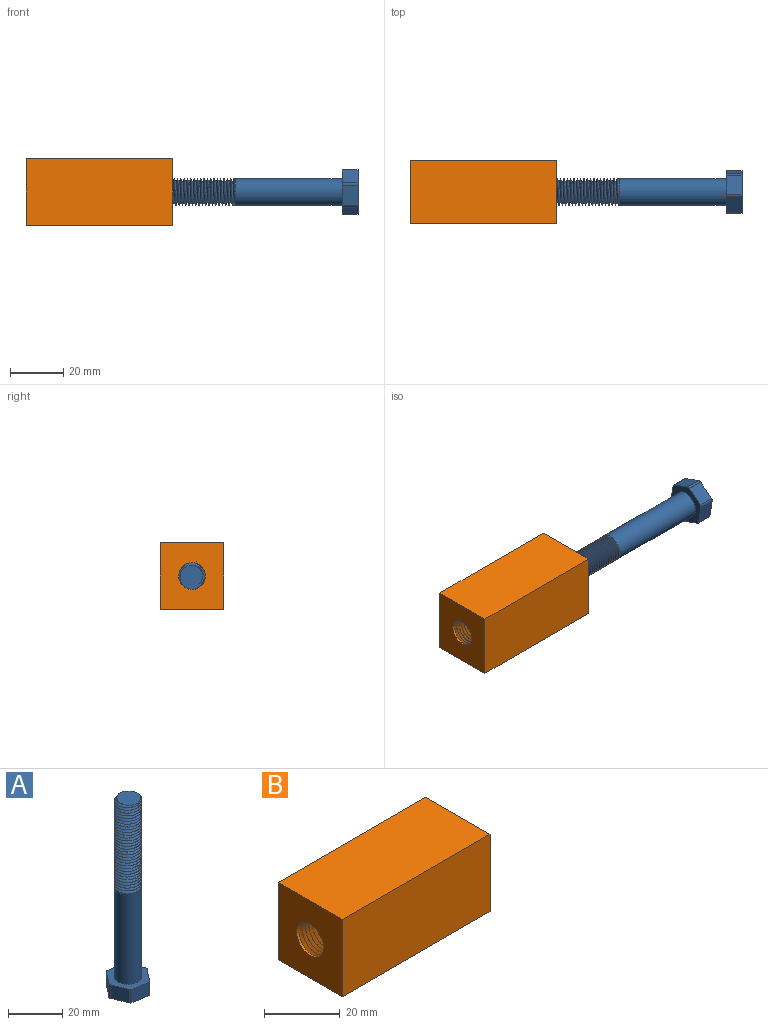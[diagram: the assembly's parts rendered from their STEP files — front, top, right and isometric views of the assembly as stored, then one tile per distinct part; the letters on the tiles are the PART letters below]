
ASSEMBLY  parts=2 mates=1
PART A: 21 faces, bbox 17.7x16.8x87.6 mm
  f0: cylinder r=5mm len=40mm, axis (0,0,-1), area -150.1mm2, adj f16,f17,f18,f19,f20
  f1: plane 7.43x6mm, normal (-0.14,-0.99,0), area 45mm2, adj f7,f8,f9,f14
  f2: plane 6x5.89mm, normal (0.78,-0.62,0), area 45mm2, adj f7,f8,f9,f10
  f3: plane 6.98x6mm, normal (0.93,0.37,0), area 45mm2, adj f7,f8,f10,f11
  f4: plane 7.43x6mm, normal (0.14,0.99,0), area 45mm2, adj f7,f8,f11,f12
  f5: plane 6x5.89mm, normal (-0.78,0.62,0), area 45mm2, adj f7,f8,f12,f13
  f6: plane 6.98x6mm, normal (-0.93,-0.37,0), area 45mm2, adj f7,f8,f13,f14
  f7: plane 16.85x15.95mm, normal (0,0,1), area 114.4mm2, adj f1,f2,f3,f4,f5,f6,f9,f10
  f8: plane 16.85x15.95mm, normal (0,0,-1), area 194.5mm2, adj f1,f2,f3,f4,f5,f6,f9,f10
  f9: cylinder r=1mm len=6mm, axis (0,0,-1), area 6.3mm2, adj f1,f2,f7,f8
  f10: cylinder r=1mm len=6mm, axis (0,0,-1), area 6.3mm2, adj f2,f3,f7,f8
  f11: cylinder r=1mm len=6mm, axis (0,0,-1), area 6.3mm2, adj f3,f4,f7,f8
  f12: cylinder r=1mm len=6mm, axis (0,0,-1), area 6.3mm2, adj f4,f5,f7,f8
  f13: cylinder r=1mm len=6mm, axis (0,0,-1), area 6.3mm2, adj f5,f6,f7,f8
  f14: cylinder r=1mm len=6mm, axis (0,0,-1), area 6.3mm2, adj f1,f6,f7,f8
  f15: cylinder r=5.05mm len=40mm, axis (0,0,-1), area 1269.2mm2, adj f7,f16
  f16: plane 10.1x10.1mm, normal (0,0,1), area 1.6mm2, adj f0,f15
  f17: plane 9.9x9.88mm, normal (0,0,1), area 64mm2, adj f0,f19,f20
  f18: plane 1.2x1.04mm, normal (0,1,0), area 0.6mm2, adj f0,f19,f20
  f19: bspline ~40.6x11.55mm, area 1070.9mm2, adj f0,f17,f18,f20
  f20: bspline ~40.18x11.55mm, area 1058mm2, adj f0,f17,f18,f19
PART B: 19 faces, bbox 57x24.8x25.8 mm
  f0: cylinder r=5.05mm len=55.25mm, axis (-1,0,0), area -140.6mm2, adj f2,f4,f7,f8,f9
  f1: plane 55.25x25mm, normal (0,-1,0), area 1381.3mm2, adj f2,f4,f5,f6
  f2: plane 25.85x24.84mm, normal (1,0,0), area 502.7mm2, adj f0,f1,f3,f5,f6,f7,f8
  f3: plane 55.25x25mm, normal (0,1,0), area 1381.3mm2, adj f2,f4,f5,f6
  f4: plane 25x23.99mm, normal (-1,0,0), area 519.6mm2, adj f0,f1,f3,f5,f6
  f5: plane 55.25x23.99mm, normal (0,0,1), area 1325.4mm2, adj f1,f2,f3,f4
  f6: plane 55.25x23.99mm, normal (0,0,-1), area 1068mm2, adj f1,f2,f3,f4,f10,f11,f12,f13
  f7: bspline ~56.02x14.06mm, area 1837.5mm2, adj f0,f2,f8,f9
  f8: bspline ~55.6x14.06mm, area 1830.8mm2, adj f0,f2,f7,f9
  f9: plane 1.2x1mm, normal (0,-0.96,-0.3), area 0.6mm2, adj f0,f7,f8
  f10: plane 2x0.81mm, normal (-1,0,0), area 1.6mm2, adj f6,f11,f17,f18
  f11: cylinder r=3mm len=3mm, axis (0,0,-1), area 9.4mm2, adj f6,f10,f12,f18
  f12: plane 22.97x2mm, normal (0,1,0), area 45.9mm2, adj f6,f11,f13,f18
  f13: cylinder r=5mm len=5mm, axis (0,0,-1), area 15.7mm2, adj f6,f12,f14,f18
  f14: plane 2x0.31mm, normal (1,0,0), area 0.6mm2, adj f6,f13,f15,f18
  f15: cylinder r=3.5mm len=3.5mm, axis (0,0,-1), area 11mm2, adj f6,f14,f16,f18
  f16: plane 22.47x2mm, normal (0,-1,0), area 44.9mm2, adj f6,f15,f17,f18
  f17: cylinder r=5mm len=5mm, axis (0,0,-1), area 15.7mm2, adj f6,f10,f16,f18
  f18: plane 30.97x8.81mm, normal (0,0,-1), area 257.4mm2, adj f10,f11,f12,f13,f14,f15,f16,f17
PLACE A rot(axis=(-0.71,-0.01,0.71),179.4deg) t=(97.19,0,-12.5)mm
PLACE B t=(0,0,-12.5)mm fixed
MATE cylindrical B.f0 <-> A.f0  axis (-1,0,0) through (27.63,0,-12.5)mm
